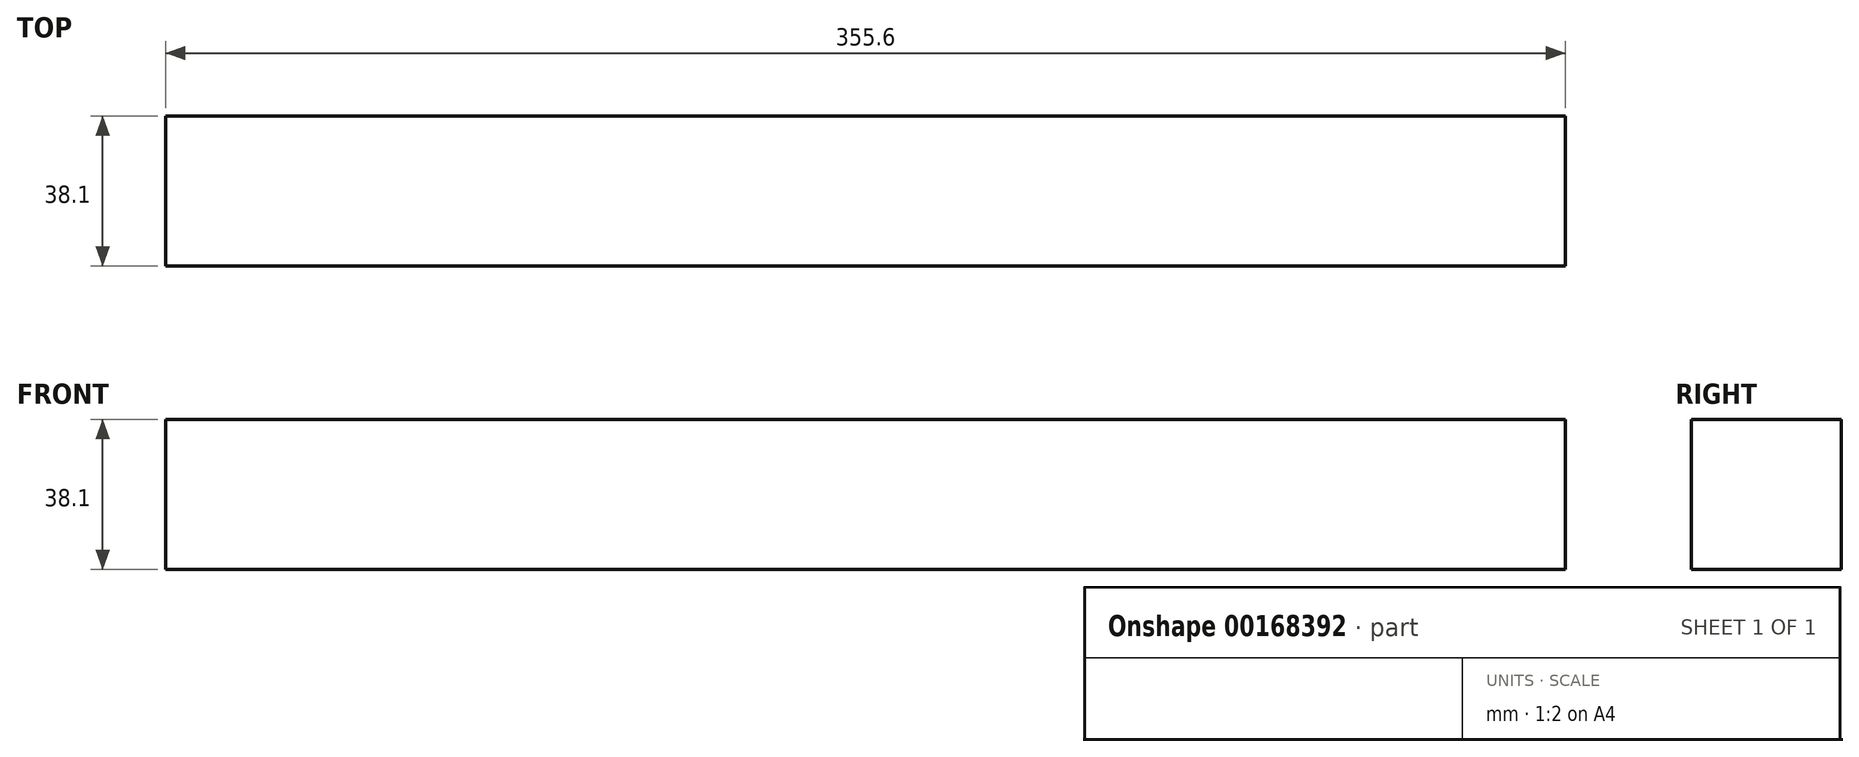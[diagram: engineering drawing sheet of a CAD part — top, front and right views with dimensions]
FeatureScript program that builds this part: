
annotation { "Feature Type Name" : "Feature", "Feature Type Description" : "" }
export const myFeature = defineFeature(function(context is Context, id is Id, definition is map)
    precondition{}
    {
        {
            var Q0;
            Q0=qCreatedBy(makeId("Top.planeOp"),FACE);
            var sketch = newSketch(context, id + "F0", { "sketchPlane" : qUnion([Q0])});
            skLineSegment(sketch, "E0.bottom", {"start": v(-177.8, 19.05) * mm, "end": v(177.8, 19.05) * mm});
            skLineSegment(sketch, "E0.top", {"start": v(-177.8, -19.05) * mm, "end": v(177.8, -19.05) * mm});
            skLineSegment(sketch, "E0.left", {"start": v(-177.8, 19.05) * mm, "end": v(-177.8, -19.05) * mm});
            skLineSegment(sketch, "E0.right", {"start": v(177.8, 19.05) * mm, "end": v(177.8, -19.05) * mm});
            skPoint(sketch, "E0.middle", {"position": v(0, 0) * mm});
            skSolve(sketch);
        }
        {
            var Q0;
            Q0=makeQuery(id+"F0.imprint","IMPRINT",FACE,{"disambiguationData":[TD([[makeQuery(id+"F0.imprint","IMPRINT",EDGE,{"derivedFrom":sQuery(id+"F0.wireOp",EDGE,"E0.bottom")}),-1.0]])]});
            extrude(context, id + "F1", {"entities" : qUnion([Q0]), "depth" : 38.1 * mm});
        }
    });
